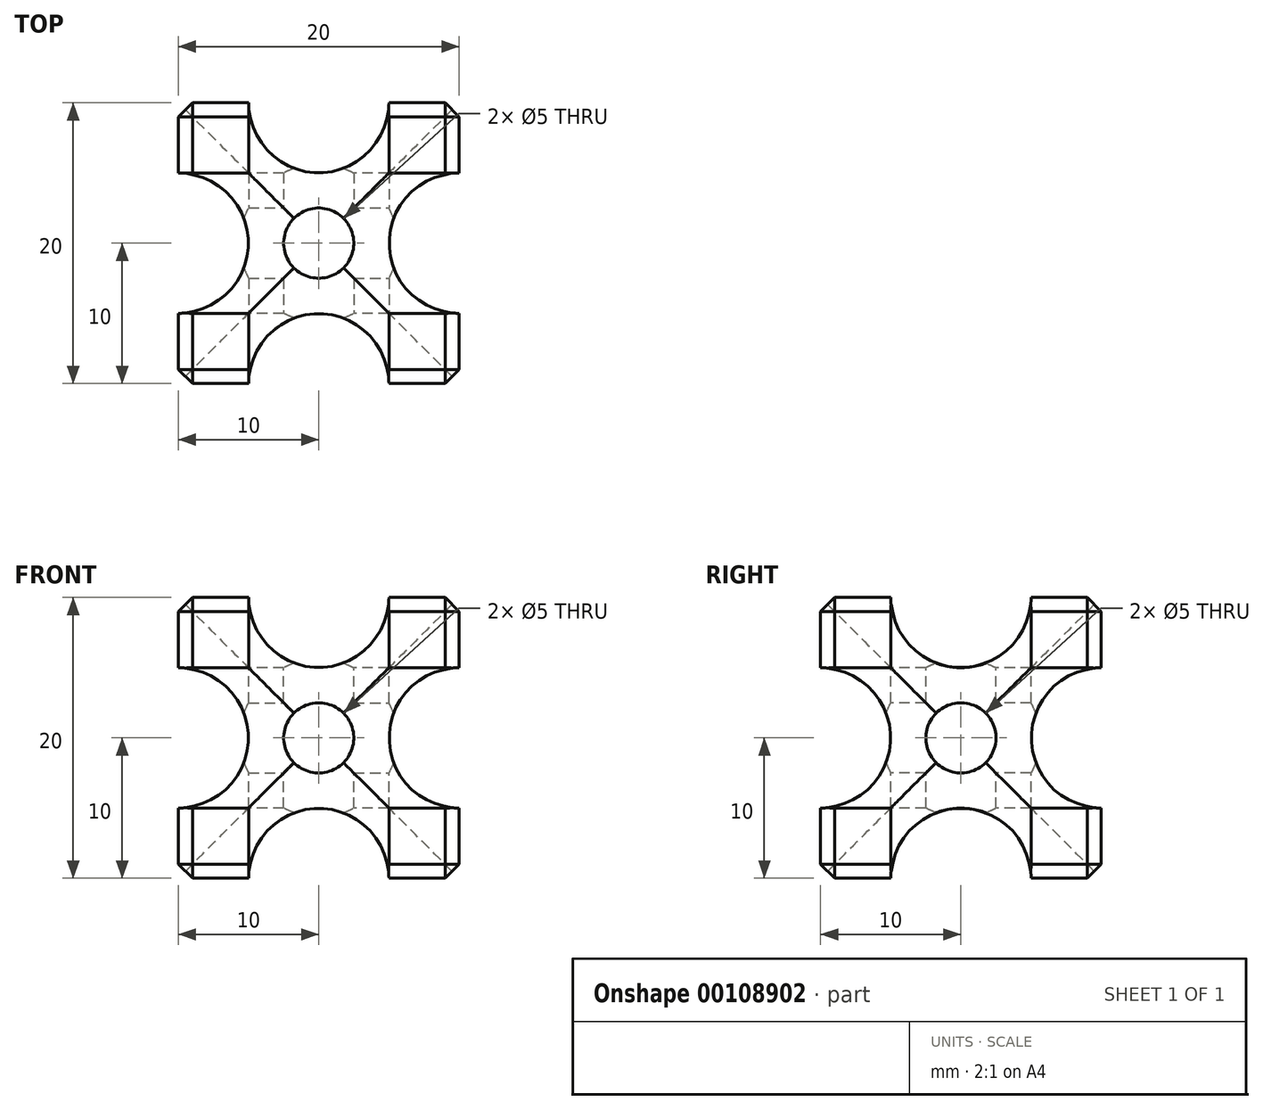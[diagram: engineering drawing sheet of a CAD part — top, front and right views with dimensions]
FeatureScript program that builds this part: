
annotation { "Feature Type Name" : "Feature", "Feature Type Description" : "" }
export const myFeature = defineFeature(function(context is Context, id is Id, definition is map)
    precondition{}
    {
        {
            var Q0;
            Q0=qCreatedBy(makeId("Top.planeOp"),FACE);
            var sketch = newSketch(context, id + "F0", { "sketchPlane" : qUnion([Q0])});
            skLineSegment(sketch, "E0.bottom", {"start": v(10, -10) * mm, "end": v(-10, -10) * mm});
            skLineSegment(sketch, "E0.top", {"start": v(10, 10) * mm, "end": v(-10, 10) * mm});
            skLineSegment(sketch, "E0.left", {"start": v(10, -10) * mm, "end": v(10, 10) * mm});
            skLineSegment(sketch, "E0.right", {"start": v(-10, -10) * mm, "end": v(-10, 10) * mm});
            skPoint(sketch, "E0.middle", {"position": v(0, 0) * mm});
            skSolve(sketch);
        }
        {
            var Q0;
            Q0=makeQuery(id+"F0.imprint","IMPRINT",FACE,{"disambiguationData":[TD([[makeQuery(id+"F0.imprint","IMPRINT",EDGE,{"derivedFrom":sQuery(id+"F0.wireOp",EDGE,"E0.bottom")}),-1.0]])]});
            extrude(context, id + "F1", {"entities" : qUnion([Q0]), "depth" : 20 * mm});
        }
        {
            var Q0;
            Q0=makeQuery(id+"F1.opExtrude","CAP_FACE",FACE,{"disambiguationData":[OSD([sQuery(id+"F0.wireOp",EDGE,"E0.bottom"),sQuery(id+"F0.wireOp",EDGE,"E0.top"),sQuery(id+"F0.wireOp",EDGE,"E0.left"),sQuery(id+"F0.wireOp",EDGE,"E0.right")])],"isStart":false});
            var sketch = newSketch(context, id + "F2", { "sketchPlane" : qUnion([Q0])});
            skPoint(sketch, "E1", {"position": v(0, 0) * mm});
            skSolve(sketch);
        }
        {
            var Q0;
            Q0=makeQuery(id+"F1.opExtrude","SWEPT_FACE",FACE,{"disambiguationData":[OSD([sQuery(id+"F0.wireOp",EDGE,"E0.bottom")])]});
            var sketch = newSketch(context, id + "F3", { "sketchPlane" : qUnion([Q0])});
            skPoint(sketch, "E2", {"position": v(0, 10) * mm});
            skPoint(sketch, "E2.positionSnap0", {"position": v(10, 10) * mm});
            skPoint(sketch, "E2.positionSnap1", {"position": v(0, 20) * mm});
            skSolve(sketch);
        }
        {
            var Q0;
            Q0=makeQuery(id+"F1.opExtrude","SWEPT_FACE",FACE,{"disambiguationData":[OSD([sQuery(id+"F0.wireOp",EDGE,"E0.left")])]});
            var sketch = newSketch(context, id + "F4", { "sketchPlane" : qUnion([Q0])});
            skPoint(sketch, "E3", {"position": v(0, 10) * mm});
            skPoint(sketch, "E3.positionSnap0", {"position": v(0, 20) * mm});
            skPoint(sketch, "E3.positionSnap1", {"position": v(-10, 10) * mm});
            skSolve(sketch);
        }
        {
            var Q0;
            Q0=sQuery(id+"F3.wireOp",VERTEX,"E2");
            var Q1;
            Q1=sQuery(id+"F2.wireOp",VERTEX,"E1");
            var Q2;
            Q2=sQuery(id+"F4.wireOp",VERTEX,"E3");
            var Q3;
            Q3=makeQuery(id+"F1.opExtrude","SWEPT_BODY",BODY,{"disambiguationData":[OSD([sQuery(id+"F0.wireOp",EDGE,"E0.bottom"),sQuery(id+"F0.wireOp",EDGE,"E0.top"),sQuery(id+"F0.wireOp",EDGE,"E0.left"),sQuery(id+"F0.wireOp",EDGE,"E0.right")])]});
            hole(context, id + "F5", {"style" : HoleStyle.SIMPLE, "endStyle" : HoleEndStyle.THROUGH, "holeDiameter" : 5 * mm, "locations" : qUnion([Q0, Q1, Q2]), "scope" : qUnion([Q3]), "isTappedThrough" : true});
        }
        {
            var Q0;
            Q0=makeQuery(id+"F1.opExtrude","SWEPT_FACE",FACE,{"disambiguationData":[OSD([sQuery(id+"F0.wireOp",EDGE,"E0.right")])]});
            var sketch = newSketch(context, id + "F6", { "sketchPlane" : qUnion([Q0])});
            skPoint(sketch, "E4", {"position": v(0, 10) * mm});
            skPoint(sketch, "E4.positionSnap0", {"position": v(-10, 10) * mm});
            skCircle(sketch, "E5", {"center": v(10, 10) * mm, "radius": 5 * mm});
            skCircle(sketch, "E6.1.0", {"center": v(0, 20) * mm, "radius": 5 * mm});
            skCircle(sketch, "E6.2.0", {"center": v(-10, 10) * mm, "radius": 5 * mm});
            skCircle(sketch, "E6.3.0", {"center": v(0, 0) * mm, "radius": 5 * mm});
            skSolve(sketch);
        }
        {
            var Q0;
            Q0=makeQuery(id+"F1.opExtrude","SWEPT_FACE",FACE,{"disambiguationData":[OSD([sQuery(id+"F0.wireOp",EDGE,"E0.bottom")])]});
            var sketch = newSketch(context, id + "F7", { "sketchPlane" : qUnion([Q0])});
            skCircle(sketch, "E7", {"center": v(0, 20) * mm, "radius": 5 * mm});
            skCircle(sketch, "E8.1.0", {"center": v(-10, 10) * mm, "radius": 5 * mm});
            skCircle(sketch, "E8.2.0", {"center": v(0, 0) * mm, "radius": 5 * mm});
            skCircle(sketch, "E8.3.0", {"center": v(10, 10) * mm, "radius": 5 * mm});
            skPoint(sketch, "E8.center", {"position": v(0, 10) * mm});
            skSolve(sketch);
        }
        {
            var Q0;
            Q0=makeQuery(id+"F1.opExtrude","CAP_FACE",FACE,{"disambiguationData":[OSD([sQuery(id+"F0.wireOp",EDGE,"E0.bottom"),sQuery(id+"F0.wireOp",EDGE,"E0.top"),sQuery(id+"F0.wireOp",EDGE,"E0.left"),sQuery(id+"F0.wireOp",EDGE,"E0.right")])],"isStart":false});
            var sketch = newSketch(context, id + "F8", { "sketchPlane" : qUnion([Q0])});
            skCircle(sketch, "E9", {"center": v(10, 0) * mm, "radius": 5 * mm});
            skCircle(sketch, "E10.1.0", {"center": v(0, 10) * mm, "radius": 5 * mm});
            skCircle(sketch, "E10.2.0", {"center": v(-10, 0) * mm, "radius": 5 * mm});
            skCircle(sketch, "E10.3.0", {"center": v(0, -10) * mm, "radius": 5 * mm});
            skPoint(sketch, "E10.center", {"position": v(0, 0) * mm});
            skSolve(sketch);
        }
        {
            var Q0;
            {var subQ0=sQuery(id+"F8.wireOp",EDGE,"E10.1.0");var subQ1=makeQuery(id+"F1.opExtrude","CAP_EDGE",EDGE,{"disambiguationData":[OSD([sQuery(id+"F0.wireOp",EDGE,"E0.top")])],"isStart":false});var subQ2=makeQuery(id+"F8.imprint","INTERSECT",VERTEX,{"disambiguationData":[OD(0.0)],"derivedFrom":[subQ1,subQ0]});Q0=makeQuery(id+"F8.imprint","IMPRINT",FACE,{"disambiguationData":[TD([[makeQuery(id+"F8.imprint","IMPRINT",EDGE,{"disambiguationData":[TD([[subQ2,1.0]])],"derivedFrom":subQ0}),1.0]])]});}
            var Q1;
            {var subQ0=sQuery(id+"F8.wireOp",EDGE,"E9");var subQ1=makeQuery(id+"F1.opExtrude","CAP_EDGE",EDGE,{"disambiguationData":[OSD([sQuery(id+"F0.wireOp",EDGE,"E0.left")])],"isStart":false});var subQ2=makeQuery(id+"F8.imprint","INTERSECT",VERTEX,{"disambiguationData":[OD(0.0)],"derivedFrom":[subQ1,subQ0]});Q1=makeQuery(id+"F8.imprint","IMPRINT",FACE,{"disambiguationData":[TD([[makeQuery(id+"F8.imprint","IMPRINT",EDGE,{"disambiguationData":[TD([[subQ2,1.0]])],"derivedFrom":subQ0}),1.0]])]});}
            var Q2;
            {var subQ0=sQuery(id+"F8.wireOp",EDGE,"E10.3.0");var subQ1=makeQuery(id+"F1.opExtrude","CAP_EDGE",EDGE,{"disambiguationData":[OSD([sQuery(id+"F0.wireOp",EDGE,"E0.bottom")])],"isStart":false});var subQ2=makeQuery(id+"F8.imprint","INTERSECT",VERTEX,{"disambiguationData":[OD(0.0)],"derivedFrom":[subQ1,subQ0]});Q2=makeQuery(id+"F8.imprint","IMPRINT",FACE,{"disambiguationData":[TD([[makeQuery(id+"F8.imprint","IMPRINT",EDGE,{"disambiguationData":[TD([[subQ2,-1.0]])],"derivedFrom":subQ0}),1.0]])]});}
            var Q3;
            {var subQ0=sQuery(id+"F8.wireOp",EDGE,"E10.2.0");var subQ1=makeQuery(id+"F1.opExtrude","CAP_EDGE",EDGE,{"disambiguationData":[OSD([sQuery(id+"F0.wireOp",EDGE,"E0.right")])],"isStart":false});var subQ2=makeQuery(id+"F8.imprint","INTERSECT",VERTEX,{"disambiguationData":[OD(0.0)],"derivedFrom":[subQ1,subQ0]});Q3=makeQuery(id+"F8.imprint","IMPRINT",FACE,{"disambiguationData":[TD([[makeQuery(id+"F8.imprint","IMPRINT",EDGE,{"disambiguationData":[TD([[subQ2,-1.0]])],"derivedFrom":subQ0}),1.0]])]});}
            extrude(context, id + "F9", {"entities" : qUnion([Q0, Q1, Q2, Q3]), "operationType" : NewBodyOperationType.REMOVE, "oppositeDirection" : true, "depth" : 25 * mm});
        }
        {
            var Q0;
            {var subQ0=sQuery(id+"F7.wireOp",EDGE,"E7");var subQ1=makeQuery(id+"F1.opExtrude","CAP_EDGE",EDGE,{"disambiguationData":[OSD([sQuery(id+"F0.wireOp",EDGE,"E0.bottom")])],"isStart":false});var subQ2=makeQuery(id+"F7.imprint","INTERSECT",VERTEX,{"disambiguationData":[OD(0.0)],"derivedFrom":[subQ1,subQ0]});Q0=makeQuery(id+"F7.imprint","IMPRINT",FACE,{"disambiguationData":[TD([[makeQuery(id+"F7.imprint","IMPRINT",EDGE,{"disambiguationData":[TD([[subQ2,1.0]])],"derivedFrom":subQ0}),1.0]])]});}
            var Q1;
            {var subQ0=sQuery(id+"F7.wireOp",EDGE,"E8.3.0");var subQ1=makeQuery(id+"F1.opExtrude","SWEPT_EDGE",EDGE,{"disambiguationData":[OSD([sQuery(id+"F0.wireOp",EDGE,"E0.bottom"),sQuery(id+"F0.wireOp",EDGE,"E0.left")])]});var subQ2=makeQuery(id+"F7.imprint","INTERSECT",VERTEX,{"disambiguationData":[OD(0.0)],"derivedFrom":[subQ1,subQ0]});Q1=makeQuery(id+"F7.imprint","IMPRINT",FACE,{"disambiguationData":[TD([[makeQuery(id+"F7.imprint","IMPRINT",EDGE,{"disambiguationData":[TD([[subQ2,1.0]])],"derivedFrom":subQ0}),1.0]])]});}
            var Q2;
            {var subQ0=sQuery(id+"F7.wireOp",EDGE,"E8.2.0");var subQ1=makeQuery(id+"F1.opExtrude","CAP_EDGE",EDGE,{"disambiguationData":[OSD([sQuery(id+"F0.wireOp",EDGE,"E0.bottom")])],"isStart":true});var subQ2=makeQuery(id+"F7.imprint","INTERSECT",VERTEX,{"disambiguationData":[OD(0.0)],"derivedFrom":[subQ1,subQ0]});Q2=makeQuery(id+"F7.imprint","IMPRINT",FACE,{"disambiguationData":[TD([[makeQuery(id+"F7.imprint","IMPRINT",EDGE,{"disambiguationData":[TD([[subQ2,-1.0]])],"derivedFrom":subQ0}),1.0]])]});}
            var Q3;
            {var subQ0=sQuery(id+"F7.wireOp",EDGE,"E8.1.0");var subQ1=makeQuery(id+"F1.opExtrude","SWEPT_EDGE",EDGE,{"disambiguationData":[OSD([sQuery(id+"F0.wireOp",EDGE,"E0.bottom"),sQuery(id+"F0.wireOp",EDGE,"E0.right")])]});var subQ2=makeQuery(id+"F7.imprint","INTERSECT",VERTEX,{"disambiguationData":[OD(0.0)],"derivedFrom":[subQ1,subQ0]});Q3=makeQuery(id+"F7.imprint","IMPRINT",FACE,{"disambiguationData":[TD([[makeQuery(id+"F7.imprint","IMPRINT",EDGE,{"disambiguationData":[TD([[subQ2,-1.0]])],"derivedFrom":subQ0}),1.0]])]});}
            extrude(context, id + "F10", {"entities" : qUnion([Q0, Q1, Q2, Q3]), "operationType" : NewBodyOperationType.REMOVE, "oppositeDirection" : true, "depth" : 25 * mm});
        }
        {
            var Q0;
            {var subQ0=sQuery(id+"F6.wireOp",EDGE,"E6.1.0");var subQ1=makeQuery(id+"F1.opExtrude","CAP_EDGE",EDGE,{"disambiguationData":[OSD([sQuery(id+"F0.wireOp",EDGE,"E0.right")])],"isStart":false});var subQ2=makeQuery(id+"F6.imprint","INTERSECT",VERTEX,{"disambiguationData":[OD(0.0)],"derivedFrom":[subQ1,subQ0]});Q0=makeQuery(id+"F6.imprint","IMPRINT",FACE,{"disambiguationData":[TD([[makeQuery(id+"F6.imprint","IMPRINT",EDGE,{"disambiguationData":[TD([[subQ2,1.0]])],"derivedFrom":subQ0}),1.0]])]});}
            var Q1;
            {var subQ0=sQuery(id+"F6.wireOp",EDGE,"E5");var subQ1=makeQuery(id+"F1.opExtrude","SWEPT_EDGE",EDGE,{"disambiguationData":[OSD([sQuery(id+"F0.wireOp",EDGE,"E0.bottom"),sQuery(id+"F0.wireOp",EDGE,"E0.right")])]});var subQ2=makeQuery(id+"F6.imprint","INTERSECT",VERTEX,{"disambiguationData":[OD(0.0)],"derivedFrom":[subQ1,subQ0]});Q1=makeQuery(id+"F6.imprint","IMPRINT",FACE,{"disambiguationData":[TD([[makeQuery(id+"F6.imprint","IMPRINT",EDGE,{"disambiguationData":[TD([[subQ2,1.0]])],"derivedFrom":subQ0}),1.0]])]});}
            var Q2;
            {var subQ0=sQuery(id+"F6.wireOp",EDGE,"E6.3.0");var subQ1=makeQuery(id+"F1.opExtrude","CAP_EDGE",EDGE,{"disambiguationData":[OSD([sQuery(id+"F0.wireOp",EDGE,"E0.right")])],"isStart":true});var subQ2=makeQuery(id+"F6.imprint","INTERSECT",VERTEX,{"disambiguationData":[OD(0.0)],"derivedFrom":[subQ1,subQ0]});Q2=makeQuery(id+"F6.imprint","IMPRINT",FACE,{"disambiguationData":[TD([[makeQuery(id+"F6.imprint","IMPRINT",EDGE,{"disambiguationData":[TD([[subQ2,-1.0]])],"derivedFrom":subQ0}),1.0]])]});}
            var Q3;
            {var subQ0=sQuery(id+"F6.wireOp",EDGE,"E6.2.0");var subQ1=makeQuery(id+"F1.opExtrude","SWEPT_EDGE",EDGE,{"disambiguationData":[OSD([sQuery(id+"F0.wireOp",EDGE,"E0.top"),sQuery(id+"F0.wireOp",EDGE,"E0.right")])]});var subQ2=makeQuery(id+"F6.imprint","INTERSECT",VERTEX,{"disambiguationData":[OD(0.0)],"derivedFrom":[subQ1,subQ0]});Q3=makeQuery(id+"F6.imprint","IMPRINT",FACE,{"disambiguationData":[TD([[makeQuery(id+"F6.imprint","IMPRINT",EDGE,{"disambiguationData":[TD([[subQ2,-1.0]])],"derivedFrom":subQ0}),1.0]])]});}
            extrude(context, id + "F11", {"entities" : qUnion([Q0, Q1, Q2, Q3]), "operationType" : NewBodyOperationType.REMOVE, "oppositeDirection" : true, "depth" : 25 * mm});
        }
        {
            var Q0;
            {var subQ0=sQuery(id+"F0.wireOp",EDGE,"E0.left");var subQ1=sQuery(id+"F0.wireOp",EDGE,"E0.top");Q0=makeQuery(id+"F9.boolean.opBoolean","SPLIT",EDGE,{"disambiguationData":[TD([makeQuery(id+"F1.opExtrude","SWEPT_FACE",FACE,{"disambiguationData":[OSD([subQ0])]})])],"derivedFrom":makeQuery(id+"F1.opExtrude","CAP_EDGE",EDGE,{"disambiguationData":[OSD([subQ1])],"isStart":true})});}
            var Q1;
            {var subQ0=sQuery(id+"F0.wireOp",EDGE,"E0.left");var subQ1=sQuery(id+"F0.wireOp",EDGE,"E0.top");Q1=makeQuery(id+"F9.boolean.opBoolean","SPLIT",EDGE,{"disambiguationData":[TD([makeQuery(id+"F1.opExtrude","SWEPT_FACE",FACE,{"disambiguationData":[OSD([subQ1])]})])],"derivedFrom":makeQuery(id+"F1.opExtrude","CAP_EDGE",EDGE,{"disambiguationData":[OSD([subQ0])],"isStart":true})});}
            var Q2;
            {var subQ0=sQuery(id+"F0.wireOp",EDGE,"E0.left");var subQ1=sQuery(id+"F0.wireOp",EDGE,"E0.top");Q2=makeQuery(id+"F10.boolean.opBoolean","SPLIT",EDGE,{"disambiguationData":[TD([makeQuery(id+"F1.opExtrude","CAP_FACE",FACE,{"disambiguationData":[OSD([sQuery(id+"F0.wireOp",EDGE,"E0.bottom"),subQ1,subQ0,sQuery(id+"F0.wireOp",EDGE,"E0.right")])],"isStart":true})])],"derivedFrom":makeQuery(id+"F1.opExtrude","SWEPT_EDGE",EDGE,{"disambiguationData":[OSD([subQ1,subQ0])]})});}
            var Q3;
            {var subQ0=sQuery(id+"F0.wireOp",EDGE,"E0.right");var subQ1=sQuery(id+"F0.wireOp",EDGE,"E0.top");Q3=makeQuery(id+"F9.boolean.opBoolean","SPLIT",EDGE,{"disambiguationData":[TD([makeQuery(id+"F1.opExtrude","SWEPT_FACE",FACE,{"disambiguationData":[OSD([subQ1])]})])],"derivedFrom":makeQuery(id+"F1.opExtrude","CAP_EDGE",EDGE,{"disambiguationData":[OSD([subQ0])],"isStart":true})});}
            var Q4;
            {var subQ0=sQuery(id+"F0.wireOp",EDGE,"E0.right");var subQ1=sQuery(id+"F0.wireOp",EDGE,"E0.top");Q4=makeQuery(id+"F9.boolean.opBoolean","SPLIT",EDGE,{"disambiguationData":[TD([makeQuery(id+"F1.opExtrude","SWEPT_FACE",FACE,{"disambiguationData":[OSD([subQ0])]})])],"derivedFrom":makeQuery(id+"F1.opExtrude","CAP_EDGE",EDGE,{"disambiguationData":[OSD([subQ1])],"isStart":true})});}
            var Q5;
            {var subQ0=sQuery(id+"F0.wireOp",EDGE,"E0.right");var subQ1=sQuery(id+"F0.wireOp",EDGE,"E0.top");Q5=makeQuery(id+"F10.boolean.opBoolean","SPLIT",EDGE,{"disambiguationData":[TD([makeQuery(id+"F1.opExtrude","CAP_FACE",FACE,{"disambiguationData":[OSD([sQuery(id+"F0.wireOp",EDGE,"E0.bottom"),subQ1,sQuery(id+"F0.wireOp",EDGE,"E0.left"),subQ0])],"isStart":true})])],"derivedFrom":makeQuery(id+"F1.opExtrude","SWEPT_EDGE",EDGE,{"disambiguationData":[OSD([subQ1,subQ0])]})});}
            var Q6;
            {var subQ0=sQuery(id+"F0.wireOp",EDGE,"E0.bottom");var subQ1=sQuery(id+"F0.wireOp",EDGE,"E0.left");Q6=makeQuery(id+"F9.boolean.opBoolean","SPLIT",EDGE,{"disambiguationData":[TD([makeQuery(id+"F1.opExtrude","SWEPT_FACE",FACE,{"disambiguationData":[OSD([subQ1])]})])],"derivedFrom":makeQuery(id+"F1.opExtrude","CAP_EDGE",EDGE,{"disambiguationData":[OSD([subQ0])],"isStart":true})});}
            var Q7;
            {var subQ0=sQuery(id+"F0.wireOp",EDGE,"E0.bottom");var subQ1=sQuery(id+"F0.wireOp",EDGE,"E0.left");Q7=makeQuery(id+"F9.boolean.opBoolean","SPLIT",EDGE,{"disambiguationData":[TD([makeQuery(id+"F1.opExtrude","SWEPT_FACE",FACE,{"disambiguationData":[OSD([subQ0])]})])],"derivedFrom":makeQuery(id+"F1.opExtrude","CAP_EDGE",EDGE,{"disambiguationData":[OSD([subQ1])],"isStart":true})});}
            var Q8;
            {var subQ0=sQuery(id+"F0.wireOp",EDGE,"E0.bottom");var subQ1=sQuery(id+"F0.wireOp",EDGE,"E0.right");Q8=makeQuery(id+"F9.boolean.opBoolean","SPLIT",EDGE,{"disambiguationData":[TD([makeQuery(id+"F1.opExtrude","SWEPT_FACE",FACE,{"disambiguationData":[OSD([subQ1])]})])],"derivedFrom":makeQuery(id+"F1.opExtrude","CAP_EDGE",EDGE,{"disambiguationData":[OSD([subQ0])],"isStart":true})});}
            var Q9;
            {var subQ0=sQuery(id+"F0.wireOp",EDGE,"E0.bottom");var subQ1=sQuery(id+"F0.wireOp",EDGE,"E0.right");Q9=makeQuery(id+"F10.boolean.opBoolean","SPLIT",EDGE,{"disambiguationData":[TD([makeQuery(id+"F1.opExtrude","CAP_FACE",FACE,{"disambiguationData":[OSD([subQ0,sQuery(id+"F0.wireOp",EDGE,"E0.top"),sQuery(id+"F0.wireOp",EDGE,"E0.left"),subQ1])],"isStart":true})])],"derivedFrom":makeQuery(id+"F1.opExtrude","SWEPT_EDGE",EDGE,{"disambiguationData":[OSD([subQ0,subQ1])]})});}
            var Q10;
            {var subQ0=sQuery(id+"F0.wireOp",EDGE,"E0.bottom");var subQ1=sQuery(id+"F0.wireOp",EDGE,"E0.right");Q10=makeQuery(id+"F9.boolean.opBoolean","SPLIT",EDGE,{"disambiguationData":[TD([makeQuery(id+"F1.opExtrude","SWEPT_FACE",FACE,{"disambiguationData":[OSD([subQ0])]})])],"derivedFrom":makeQuery(id+"F1.opExtrude","CAP_EDGE",EDGE,{"disambiguationData":[OSD([subQ1])],"isStart":true})});}
            var Q11;
            {var subQ0=sQuery(id+"F0.wireOp",EDGE,"E0.right");var subQ1=sQuery(id+"F0.wireOp",EDGE,"E0.top");Q11=makeQuery(id+"F10.boolean.opBoolean","SPLIT",EDGE,{"disambiguationData":[TD([makeQuery(id+"F1.opExtrude","CAP_FACE",FACE,{"disambiguationData":[OSD([sQuery(id+"F0.wireOp",EDGE,"E0.bottom"),subQ1,sQuery(id+"F0.wireOp",EDGE,"E0.left"),subQ0])],"isStart":false})])],"derivedFrom":makeQuery(id+"F1.opExtrude","SWEPT_EDGE",EDGE,{"disambiguationData":[OSD([subQ1,subQ0])]})});}
            var Q12;
            {var subQ0=sQuery(id+"F0.wireOp",EDGE,"E0.right");var subQ1=sQuery(id+"F0.wireOp",EDGE,"E0.top");Q12=makeQuery(id+"F9.boolean.opBoolean","SPLIT",EDGE,{"disambiguationData":[TD([makeQuery(id+"F1.opExtrude","SWEPT_FACE",FACE,{"disambiguationData":[OSD([subQ1])]})])],"derivedFrom":makeQuery(id+"F1.opExtrude","CAP_EDGE",EDGE,{"disambiguationData":[OSD([subQ0])],"isStart":false})});}
            var Q13;
            {var subQ0=sQuery(id+"F0.wireOp",EDGE,"E0.right");var subQ1=sQuery(id+"F0.wireOp",EDGE,"E0.top");Q13=makeQuery(id+"F9.boolean.opBoolean","SPLIT",EDGE,{"disambiguationData":[TD([makeQuery(id+"F1.opExtrude","SWEPT_FACE",FACE,{"disambiguationData":[OSD([subQ0])]})])],"derivedFrom":makeQuery(id+"F1.opExtrude","CAP_EDGE",EDGE,{"disambiguationData":[OSD([subQ1])],"isStart":false})});}
            var Q14;
            {var subQ0=sQuery(id+"F0.wireOp",EDGE,"E0.left");var subQ1=sQuery(id+"F0.wireOp",EDGE,"E0.top");Q14=makeQuery(id+"F9.boolean.opBoolean","SPLIT",EDGE,{"disambiguationData":[TD([makeQuery(id+"F1.opExtrude","SWEPT_FACE",FACE,{"disambiguationData":[OSD([subQ0])]})])],"derivedFrom":makeQuery(id+"F1.opExtrude","CAP_EDGE",EDGE,{"disambiguationData":[OSD([subQ1])],"isStart":false})});}
            var Q15;
            {var subQ0=sQuery(id+"F0.wireOp",EDGE,"E0.left");var subQ1=sQuery(id+"F0.wireOp",EDGE,"E0.top");Q15=makeQuery(id+"F10.boolean.opBoolean","SPLIT",EDGE,{"disambiguationData":[TD([makeQuery(id+"F1.opExtrude","CAP_FACE",FACE,{"disambiguationData":[OSD([sQuery(id+"F0.wireOp",EDGE,"E0.bottom"),subQ1,subQ0,sQuery(id+"F0.wireOp",EDGE,"E0.right")])],"isStart":false})])],"derivedFrom":makeQuery(id+"F1.opExtrude","SWEPT_EDGE",EDGE,{"disambiguationData":[OSD([subQ1,subQ0])]})});}
            var Q16;
            {var subQ0=sQuery(id+"F0.wireOp",EDGE,"E0.left");var subQ1=sQuery(id+"F0.wireOp",EDGE,"E0.top");Q16=makeQuery(id+"F9.boolean.opBoolean","SPLIT",EDGE,{"disambiguationData":[TD([makeQuery(id+"F1.opExtrude","SWEPT_FACE",FACE,{"disambiguationData":[OSD([subQ1])]})])],"derivedFrom":makeQuery(id+"F1.opExtrude","CAP_EDGE",EDGE,{"disambiguationData":[OSD([subQ0])],"isStart":false})});}
            var Q17;
            {var subQ0=sQuery(id+"F0.wireOp",EDGE,"E0.bottom");var subQ1=sQuery(id+"F0.wireOp",EDGE,"E0.left");Q17=makeQuery(id+"F9.boolean.opBoolean","SPLIT",EDGE,{"disambiguationData":[TD([makeQuery(id+"F1.opExtrude","SWEPT_FACE",FACE,{"disambiguationData":[OSD([subQ1])]})])],"derivedFrom":makeQuery(id+"F1.opExtrude","CAP_EDGE",EDGE,{"disambiguationData":[OSD([subQ0])],"isStart":false})});}
            var Q18;
            {var subQ0=sQuery(id+"F0.wireOp",EDGE,"E0.bottom");var subQ1=sQuery(id+"F0.wireOp",EDGE,"E0.left");Q18=makeQuery(id+"F9.boolean.opBoolean","SPLIT",EDGE,{"disambiguationData":[TD([makeQuery(id+"F1.opExtrude","SWEPT_FACE",FACE,{"disambiguationData":[OSD([subQ0])]})])],"derivedFrom":makeQuery(id+"F1.opExtrude","CAP_EDGE",EDGE,{"disambiguationData":[OSD([subQ1])],"isStart":false})});}
            var Q19;
            {var subQ0=sQuery(id+"F0.wireOp",EDGE,"E0.bottom");var subQ1=sQuery(id+"F0.wireOp",EDGE,"E0.right");Q19=makeQuery(id+"F9.boolean.opBoolean","SPLIT",EDGE,{"disambiguationData":[TD([makeQuery(id+"F1.opExtrude","SWEPT_FACE",FACE,{"disambiguationData":[OSD([subQ0])]})])],"derivedFrom":makeQuery(id+"F1.opExtrude","CAP_EDGE",EDGE,{"disambiguationData":[OSD([subQ1])],"isStart":false})});}
            var Q20;
            {var subQ0=sQuery(id+"F0.wireOp",EDGE,"E0.bottom");var subQ1=sQuery(id+"F0.wireOp",EDGE,"E0.right");Q20=makeQuery(id+"F10.boolean.opBoolean","SPLIT",EDGE,{"disambiguationData":[TD([makeQuery(id+"F1.opExtrude","CAP_FACE",FACE,{"disambiguationData":[OSD([subQ0,sQuery(id+"F0.wireOp",EDGE,"E0.top"),sQuery(id+"F0.wireOp",EDGE,"E0.left"),subQ1])],"isStart":false})])],"derivedFrom":makeQuery(id+"F1.opExtrude","SWEPT_EDGE",EDGE,{"disambiguationData":[OSD([subQ0,subQ1])]})});}
            var Q21;
            {var subQ0=sQuery(id+"F0.wireOp",EDGE,"E0.bottom");var subQ1=sQuery(id+"F0.wireOp",EDGE,"E0.right");Q21=makeQuery(id+"F9.boolean.opBoolean","SPLIT",EDGE,{"disambiguationData":[TD([makeQuery(id+"F1.opExtrude","SWEPT_FACE",FACE,{"disambiguationData":[OSD([subQ1])]})])],"derivedFrom":makeQuery(id+"F1.opExtrude","CAP_EDGE",EDGE,{"disambiguationData":[OSD([subQ0])],"isStart":false})});}
            var Q22;
            {var subQ0=sQuery(id+"F0.wireOp",EDGE,"E0.bottom");var subQ1=sQuery(id+"F0.wireOp",EDGE,"E0.left");Q22=makeQuery(id+"F10.boolean.opBoolean","SPLIT",EDGE,{"disambiguationData":[TD([makeQuery(id+"F1.opExtrude","CAP_FACE",FACE,{"disambiguationData":[OSD([subQ0,sQuery(id+"F0.wireOp",EDGE,"E0.top"),subQ1,sQuery(id+"F0.wireOp",EDGE,"E0.right")])],"isStart":true})])],"derivedFrom":makeQuery(id+"F1.opExtrude","SWEPT_EDGE",EDGE,{"disambiguationData":[OSD([subQ0,subQ1])]})});}
            var Q23;
            {var subQ0=sQuery(id+"F0.wireOp",EDGE,"E0.bottom");var subQ1=sQuery(id+"F0.wireOp",EDGE,"E0.left");Q23=makeQuery(id+"F10.boolean.opBoolean","SPLIT",EDGE,{"disambiguationData":[TD([makeQuery(id+"F1.opExtrude","CAP_FACE",FACE,{"disambiguationData":[OSD([subQ0,sQuery(id+"F0.wireOp",EDGE,"E0.top"),subQ1,sQuery(id+"F0.wireOp",EDGE,"E0.right")])],"isStart":false})])],"derivedFrom":makeQuery(id+"F1.opExtrude","SWEPT_EDGE",EDGE,{"disambiguationData":[OSD([subQ0,subQ1])]})});}
            chamfer(context, id + "F12", {"entities" : qUnion([Q0, Q1, Q2, Q3, Q4, Q5, Q6, Q7, Q8, Q9, Q10, Q11, Q12, Q13, Q14, Q15, Q16, Q17, Q18, Q19, Q20, Q21, Q22, Q23]), "width" : 1 * mm, "tangentPropagation" : true});
        }
    });
